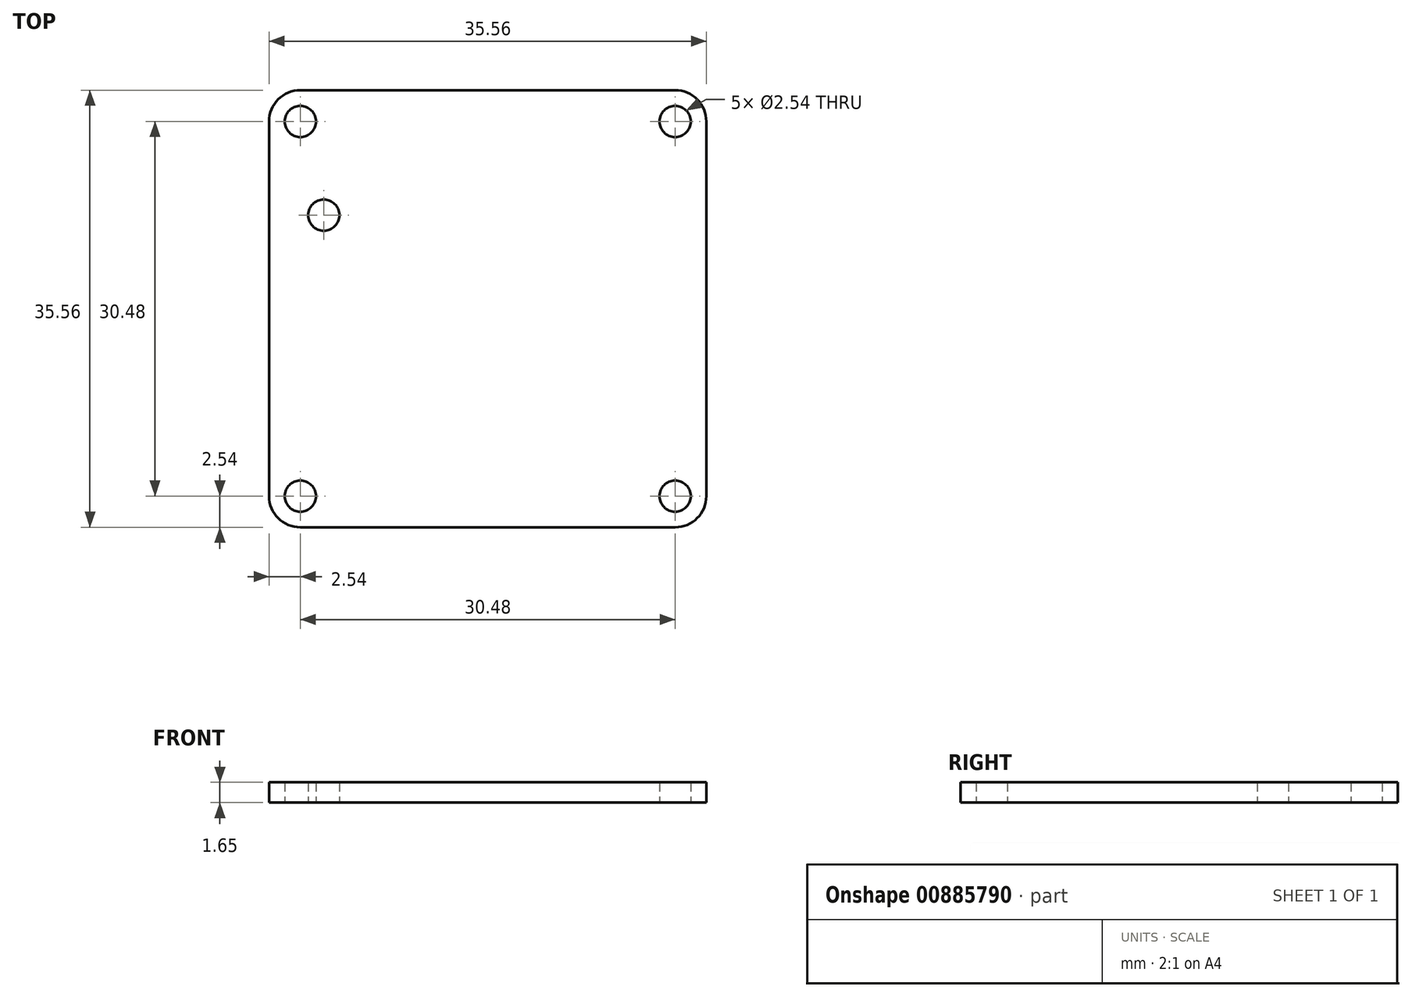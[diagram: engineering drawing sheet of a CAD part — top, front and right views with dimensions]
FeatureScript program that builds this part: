
annotation { "Feature Type Name" : "Feature", "Feature Type Description" : "" }
export const myFeature = defineFeature(function(context is Context, id is Id, definition is map)
    precondition{}
    {
        {
            var Q0;
            Q0=qCreatedBy(makeId("Top.planeOp"),FACE);
            var sketch = newSketch(context, id + "F0", { "sketchPlane" : qUnion([Q0])});
            skLineSegment(sketch, "E0.bottom", {"start": v(15.24, -15.24) * mm, "end": v(-15.24, -15.24) * mm, "construction": true});
            skLineSegment(sketch, "E0.top", {"start": v(15.24, 15.24) * mm, "end": v(-15.24, 15.24) * mm, "construction": true});
            skLineSegment(sketch, "E0.left", {"start": v(15.24, -15.24) * mm, "end": v(15.24, 15.24) * mm, "construction": true});
            skLineSegment(sketch, "E0.right", {"start": v(-15.24, -15.24) * mm, "end": v(-15.24, 15.24) * mm, "construction": true});
            skPoint(sketch, "E0.middle", {"position": v(0, 0) * mm});
            skCircle(sketch, "E1", {"center": v(-15.24, 15.24) * mm, "radius": 1.27 * mm});
            skCircle(sketch, "E2", {"center": v(15.24, 15.24) * mm, "radius": 1.27 * mm});
            skCircle(sketch, "E3", {"center": v(15.24, -15.24) * mm, "radius": 1.27 * mm});
            skCircle(sketch, "E4", {"center": v(-15.24, -15.24) * mm, "radius": 1.27 * mm});
            skLineSegment(sketch, "E5.bottom", {"start": v(17.78, -17.78) * mm, "end": v(-17.78, -17.78) * mm});
            skLineSegment(sketch, "E5.top", {"start": v(17.78, 17.78) * mm, "end": v(-17.78, 17.78) * mm});
            skLineSegment(sketch, "E5.left", {"start": v(17.78, -17.78) * mm, "end": v(17.78, 17.78) * mm});
            skLineSegment(sketch, "E5.right", {"start": v(-17.78, -17.78) * mm, "end": v(-17.78, 17.78) * mm});
            skCircle(sketch, "E6", {"center": v(-13.33, 7.62) * mm, "radius": 1.27 * mm});
            skSolve(sketch);
        }
        {
            var Q0;
            Q0=makeQuery(id+"F0.imprint","IMPRINT",FACE,{"disambiguationData":[TD([[makeQuery(id+"F0.imprint","IMPRINT",EDGE,{"derivedFrom":sQuery(id+"F0.wireOp",EDGE,"E1")}),-1.0]])]});
            extrude(context, id + "F1", {"entities" : qUnion([Q0]), "depth" : 1.65 * mm, "offsetDistance" : 25.4 * mm});
        }
        {
            var Q0;
            Q0=makeQuery(id+"F1.opExtrude","SWEPT_EDGE",EDGE,{"disambiguationData":[OSD([sQuery(id+"F0.wireOp",EDGE,"E5.top"),sQuery(id+"F0.wireOp",EDGE,"E5.right")])]});
            var Q1;
            Q1=makeQuery(id+"F1.opExtrude","SWEPT_EDGE",EDGE,{"disambiguationData":[OSD([sQuery(id+"F0.wireOp",EDGE,"E5.bottom"),sQuery(id+"F0.wireOp",EDGE,"E5.right")])]});
            var Q2;
            Q2=makeQuery(id+"F1.opExtrude","SWEPT_EDGE",EDGE,{"disambiguationData":[OSD([sQuery(id+"F0.wireOp",EDGE,"E5.bottom"),sQuery(id+"F0.wireOp",EDGE,"E5.left")])]});
            var Q3;
            Q3=makeQuery(id+"F1.opExtrude","SWEPT_EDGE",EDGE,{"disambiguationData":[OSD([sQuery(id+"F0.wireOp",EDGE,"E5.top"),sQuery(id+"F0.wireOp",EDGE,"E5.left")])]});
            fillet(context, id + "F2", {"entities" : qUnion([Q0, Q1, Q2, Q3]), "radius" : 2.54 * mm, "tangentPropagation" : true, "allowEdgeOverflow" : false});
        }
    });
